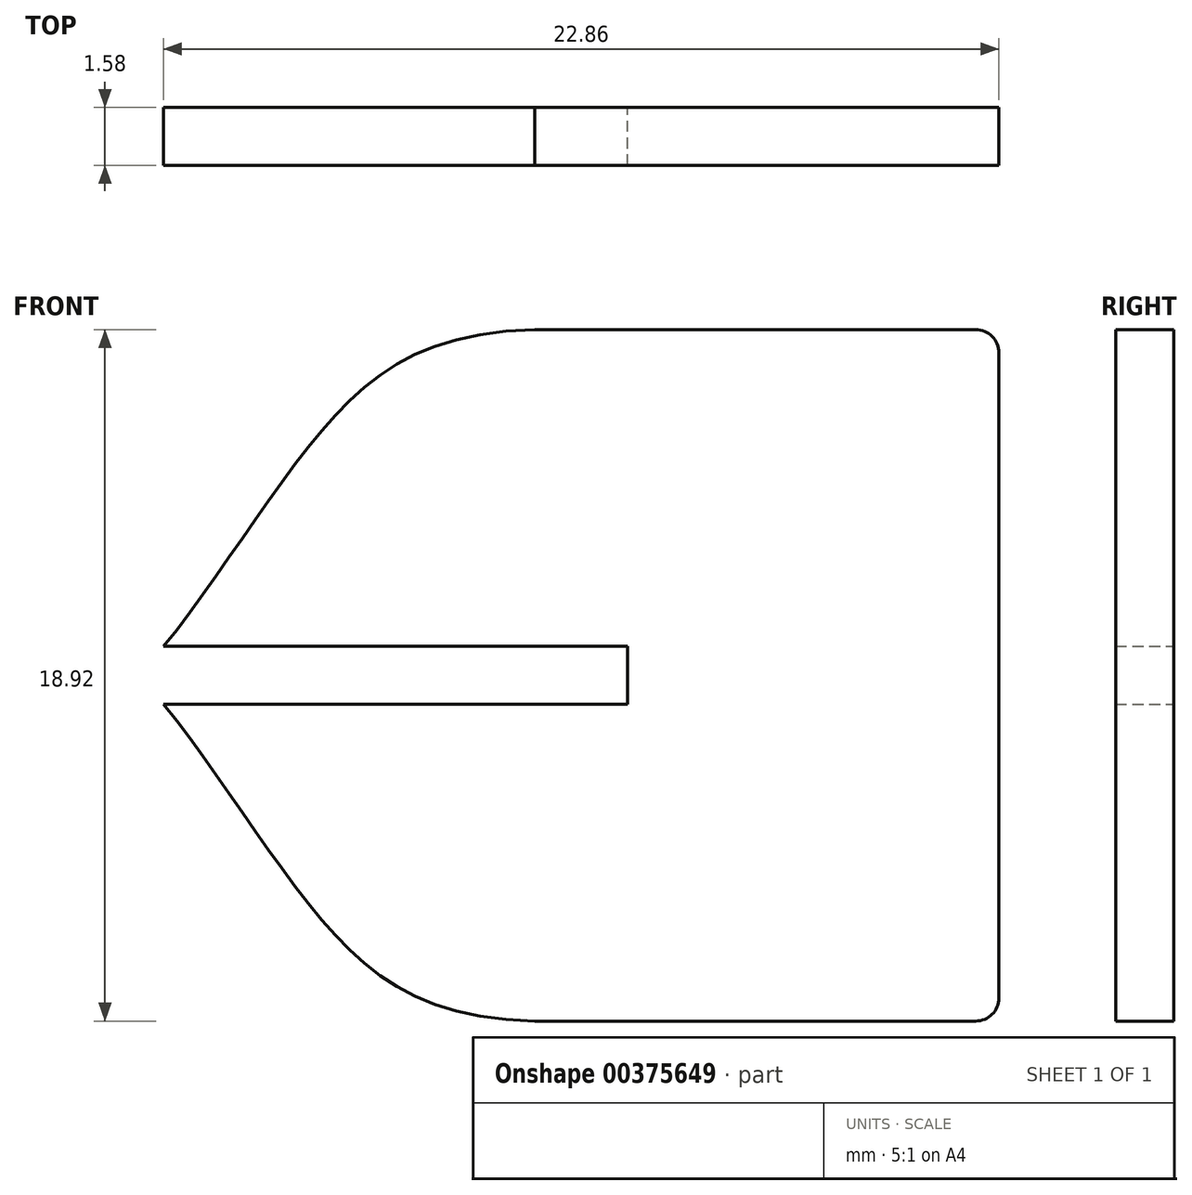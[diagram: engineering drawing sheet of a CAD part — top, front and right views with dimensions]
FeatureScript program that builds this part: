
annotation { "Feature Type Name" : "Feature", "Feature Type Description" : "" }
export const myFeature = defineFeature(function(context is Context, id is Id, definition is map)
    precondition{}
    {
        {
            var Q0;
            Q0=qCreatedBy(makeId("Front.planeOp"),FACE);
            var sketch = newSketch(context, id + "F0", { "sketchPlane" : qUnion([Q0])});
            skLineSegment(sketch, "E0", {"start": v(-22.9, 0) * mm, "end": v(14.27, 0) * mm, "construction": true});
            skLineSegment(sketch, "E1.bottom", {"start": v(6.35, -9.46) * mm, "end": v(-6.35, -9.46) * mm});
            skLineSegment(sketch, "E1.top", {"start": v(6.35, 9.46) * mm, "end": v(-6.35, 9.46) * mm});
            skLineSegment(sketch, "E1.left", {"start": v(6.35, -9.46) * mm, "end": v(6.35, 9.46) * mm});
            skPoint(sketch, "E1.middle", {"position": v(0, 0) * mm});
            skLineSegment(sketch, "E2", {"start": v(-16.51, 0.8) * mm, "end": v(-3.81, 0.8) * mm});
            skLineSegment(sketch, "E3", {"start": v(-3.81, 0.8) * mm, "end": v(-3.81, -0.8) * mm});
            skLineSegment(sketch, "E4", {"start": v(-3.81, -0.8) * mm, "end": v(-16.51, -0.8) * mm});
            skPoint(sketch, "E5.MirrorCS.start.orphan", {"position": v(-6.35, -9.46) * mm});
            skFitSpline(sketch, "E6", {"points": [v(-6.35, 9.46) * mm, v(-12.27, 6.58) * mm, v(-16.51, 0.8) * mm], "startDerivative": vector(-18.85, -0.47) * mm, "endDerivative": vector(-8.33, -10.14) * mm});
            skFitSpline(sketch, "E7.MirrorCS", {"points": [v(-6.35, -9.46) * mm, v(-12.27, -6.58) * mm, v(-16.51, -0.8) * mm], "startDerivative": vector(-18.85, 0.47) * mm, "endDerivative": vector(-8.33, 10.14) * mm});
            skSolve(sketch);
        }
        {
            var Q0;
            Q0 = qSketchRegion(id + "F0", true);
            extrude(context, id + "F1", {"entities" : qUnion([Q0]), "endBound" : BoundingType.SYMMETRIC, "depth" : 1.59 * mm});
        }
        {
            var Q0;
            Q0=makeQuery(id+"F1.opExtrude","SWEPT_EDGE",EDGE,{"disambiguationData":[OSD([sQuery(id+"F0.wireOp",EDGE,"E1.top"),sQuery(id+"F0.wireOp",EDGE,"E1.left")])]});
            var Q1;
            Q1=makeQuery(id+"F1.opExtrude","SWEPT_EDGE",EDGE,{"disambiguationData":[OSD([sQuery(id+"F0.wireOp",EDGE,"E1.bottom"),sQuery(id+"F0.wireOp",EDGE,"E1.left")])]});
            fillet(context, id + "F2", {"entities" : qUnion([Q0, Q1]), "radius" : 0.64 * mm, "tangentPropagation" : true, "allowEdgeOverflow" : false});
        }
    });
